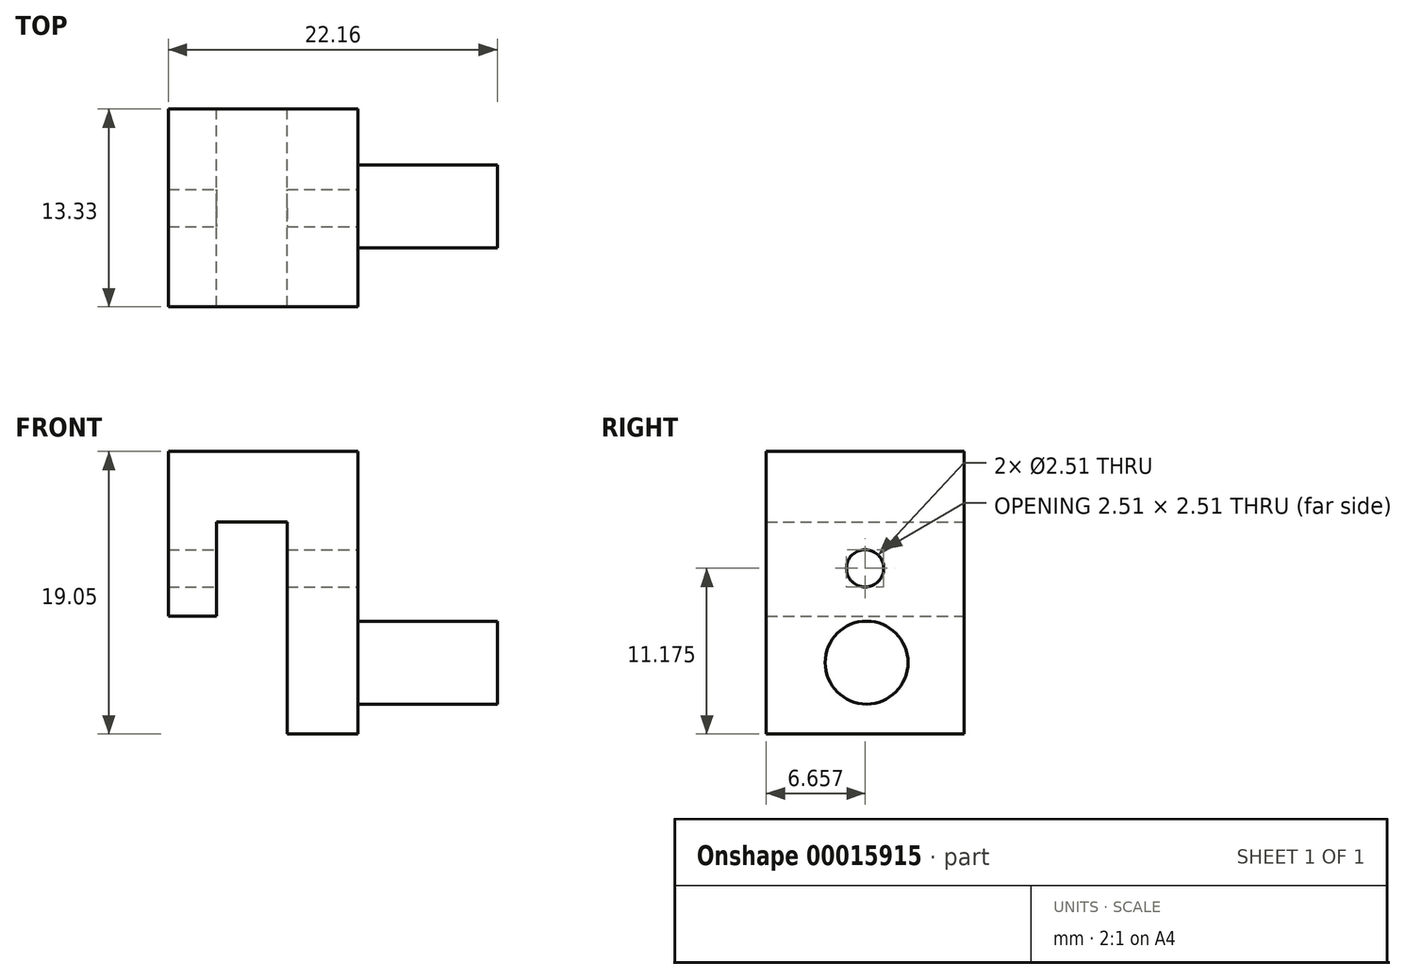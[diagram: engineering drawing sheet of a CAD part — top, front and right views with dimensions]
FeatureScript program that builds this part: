
annotation { "Feature Type Name" : "Feature", "Feature Type Description" : "" }
export const myFeature = defineFeature(function(context is Context, id is Id, definition is map)
    precondition{}
    {
        {
            var Q0;
            Q0=qCreatedBy(makeId("Front.planeOp"),FACE);
            var sketch = newSketch(context, id + "F0", { "sketchPlane" : qUnion([Q0])});
            skLineSegment(sketch, "E0", {"start": v(0, 0) * mm, "end": v(0, 4.76) * mm});
            skLineSegment(sketch, "E1", {"start": v(0, 4.76) * mm, "end": v(12.76, 4.76) * mm});
            skLineSegment(sketch, "E2", {"start": v(12.76, 4.76) * mm, "end": v(12.76, -14.29) * mm});
            skLineSegment(sketch, "E3", {"start": v(12.76, -14.29) * mm, "end": v(8, -14.29) * mm});
            skLineSegment(sketch, "E4", {"start": v(8, -14.29) * mm, "end": v(8, 0) * mm});
            skLineSegment(sketch, "E5", {"start": v(8, 0) * mm, "end": v(3.24, 0) * mm});
            skLineSegment(sketch, "E6", {"start": v(3.24, 0) * mm, "end": v(3.24, -6.35) * mm});
            skLineSegment(sketch, "E7", {"start": v(3.24, -6.35) * mm, "end": v(0, -6.35) * mm});
            skLineSegment(sketch, "E8", {"start": v(0, -6.35) * mm, "end": v(0, 0) * mm});
            skSolve(sketch);
        }
        {
            var Q0;
            Q0 = qSketchRegion(id + "F0", true);
            extrude(context, id + "F1", {"entities" : qUnion([Q0]), "depth" : 13.33 * mm});
        }
        {
            var Q0;
            Q0=makeQuery(id+"F1.opExtrude","SWEPT_FACE",FACE,{"disambiguationData":[OSD([sQuery(id+"F0.wireOp",EDGE,"E2")])]});
            var sketch = newSketch(context, id + "F2", { "sketchPlane" : qUnion([Q0])});
            skCircle(sketch, "E9", {"center": v(-6.57, -9.47) * mm, "radius": 2.8 * mm});
            skSolve(sketch);
        }
        {
            var Q0;
            Q0 = qSketchRegion(id + "F2", true);
            extrude(context, id + "F3", {"entities" : qUnion([Q0]), "operationType" : NewBodyOperationType.ADD, "depth" : 9.4 * mm});
        }
        {
            var Q0;
            Q0=makeQuery(id+"F1.opExtrude","SWEPT_FACE",FACE,{"disambiguationData":[OSD([sQuery(id+"F0.wireOp",EDGE,"E2")])]});
            var sketch = newSketch(context, id + "F4", { "sketchPlane" : qUnion([Q0])});
            skCircle(sketch, "E10", {"center": v(-6.67, -3.11) * mm, "radius": 1.26 * mm});
            skSolve(sketch);
        }
        {
            var Q0;
            Q0 = qSketchRegion(id + "F4", true);
            extrude(context, id + "F5", {"entities" : qUnion([Q0]), "operationType" : NewBodyOperationType.REMOVE, "oppositeDirection" : true, "depth" : 25.4 * mm});
        }
    });
